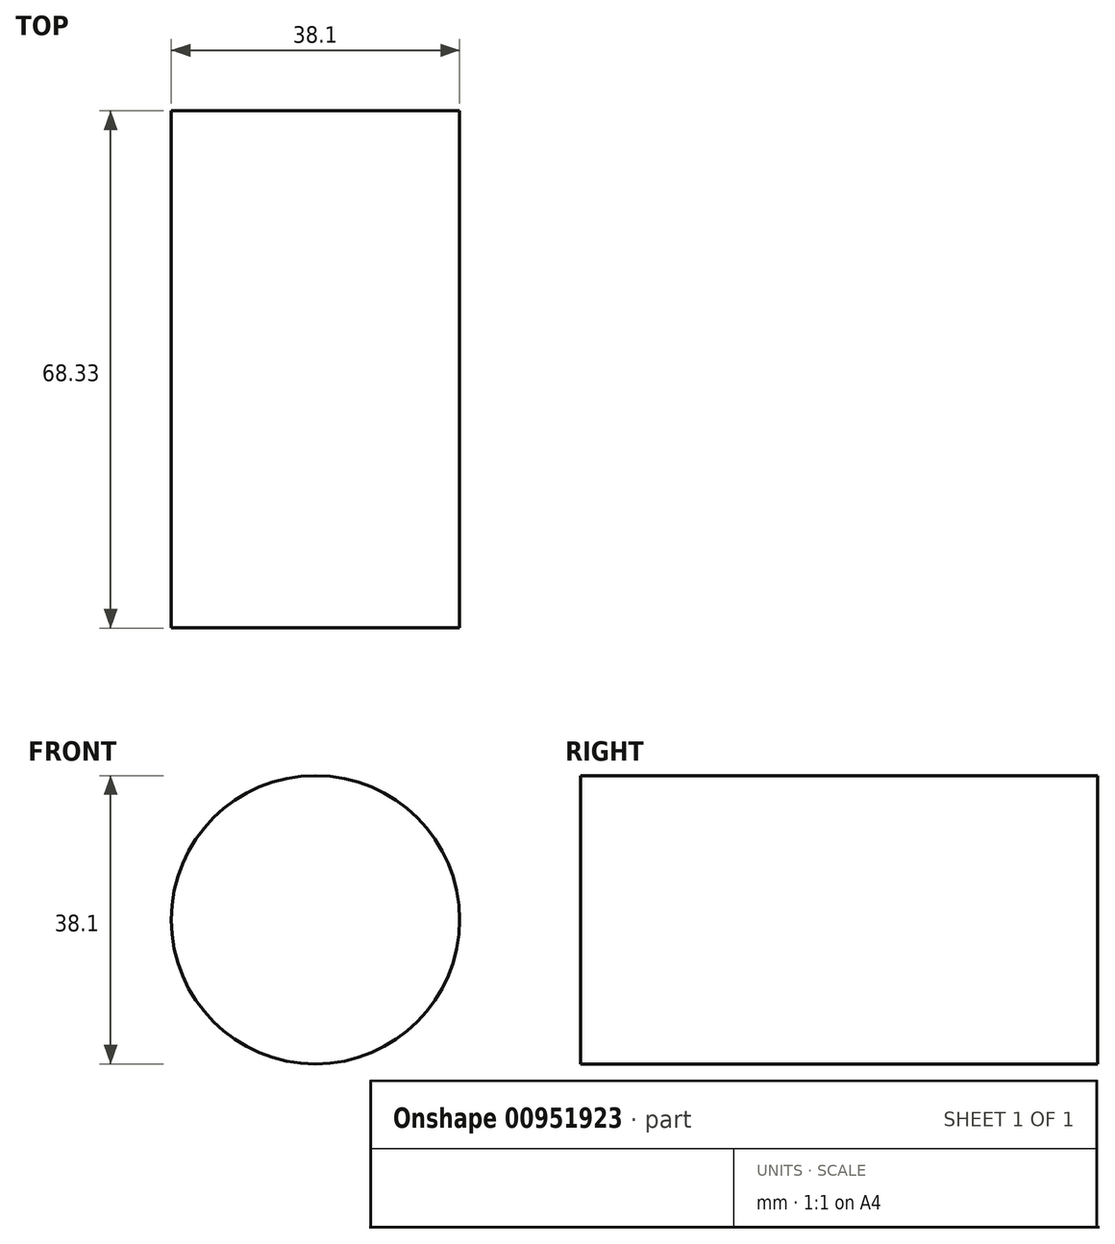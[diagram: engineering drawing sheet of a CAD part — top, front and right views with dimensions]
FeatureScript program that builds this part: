
annotation { "Feature Type Name" : "Feature", "Feature Type Description" : "" }
export const myFeature = defineFeature(function(context is Context, id is Id, definition is map)
    precondition{}
    {
        {
            var Q0;
            Q0=qCreatedBy(makeId("Front.planeOp"),FACE);
            var sketch = newSketch(context, id + "F0", { "sketchPlane" : qUnion([Q0])});
            skCircle(sketch, "E0", {"center": v(0, 0) * mm, "radius": 19.05 * mm});
            skSolve(sketch);
        }
        {
            var Q0;
            Q0 = qSketchRegion(id + "F0", true);
            extrude(context, id + "F1", {"entities" : qUnion([Q0]), "depth" : 68.33 * mm, "offsetDistance" : 25.4 * mm});
        }
    });
